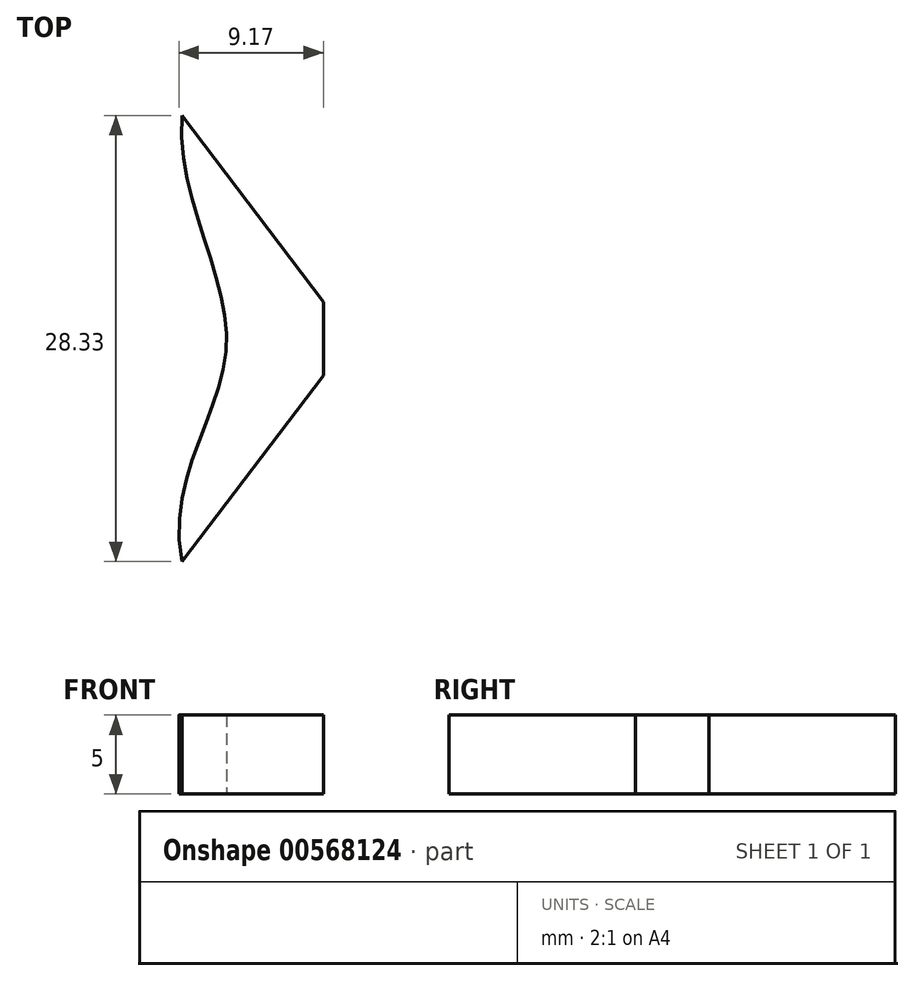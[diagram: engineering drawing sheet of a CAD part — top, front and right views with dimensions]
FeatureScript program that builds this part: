
annotation { "Feature Type Name" : "Feature", "Feature Type Description" : "" }
export const myFeature = defineFeature(function(context is Context, id is Id, definition is map)
    precondition{}
    {
        {
            var Q0;
            Q0=qCreatedBy(makeId("Top.planeOp"),FACE);
            var sketch = newSketch(context, id + "F0", { "sketchPlane" : qUnion([Q0])});
            skLineSegment(sketch, "E0", {"start": v(-30.4, 34.28) * mm, "end": v(-30.4, 29.6) * mm});
            skLineSegment(sketch, "E1", {"start": v(-30.4, 29.6) * mm, "end": v(-39.37, 17.78) * mm});
            skLineSegment(sketch, "E2.MirrorCS", {"start": v(-30.4, 29.6) * mm, "end": v(-30.4, 34.28) * mm});
            skLineSegment(sketch, "E3.MirrorCS", {"start": v(-30.4, 34.28) * mm, "end": v(-39.37, 46.1) * mm});
            skFitSpline(sketch, "E4", {"points": [v(-39.37, 46.1) * mm, v(-36.55, 31.5) * mm, v(-39.37, 17.78) * mm], "startDerivative": vector(-2.32, -31.2) * mm, "endDerivative": vector(6.43, -32.74) * mm});
            skSolve(sketch);
        }
        {
            var Q0;
            Q0 = qSketchRegion(id + "F0", true);
            extrude(context, id + "F1", {"entities" : qUnion([Q0]), "endBound" : BoundingType.SYMMETRIC, "depth" : 5 * mm, "offsetDistance" : 25 * mm});
        }
        {
            var Q0;
            Q0 = qSketchRegion(id + "F0", true);
            extrude(context, id + "F2", {"entities" : qUnion([Q0]), "operationType" : NewBodyOperationType.ADD, "endBound" : BoundingType.SYMMETRIC, "depth" : 5 * mm, "offsetDistance" : 25 * mm});
        }
    });
